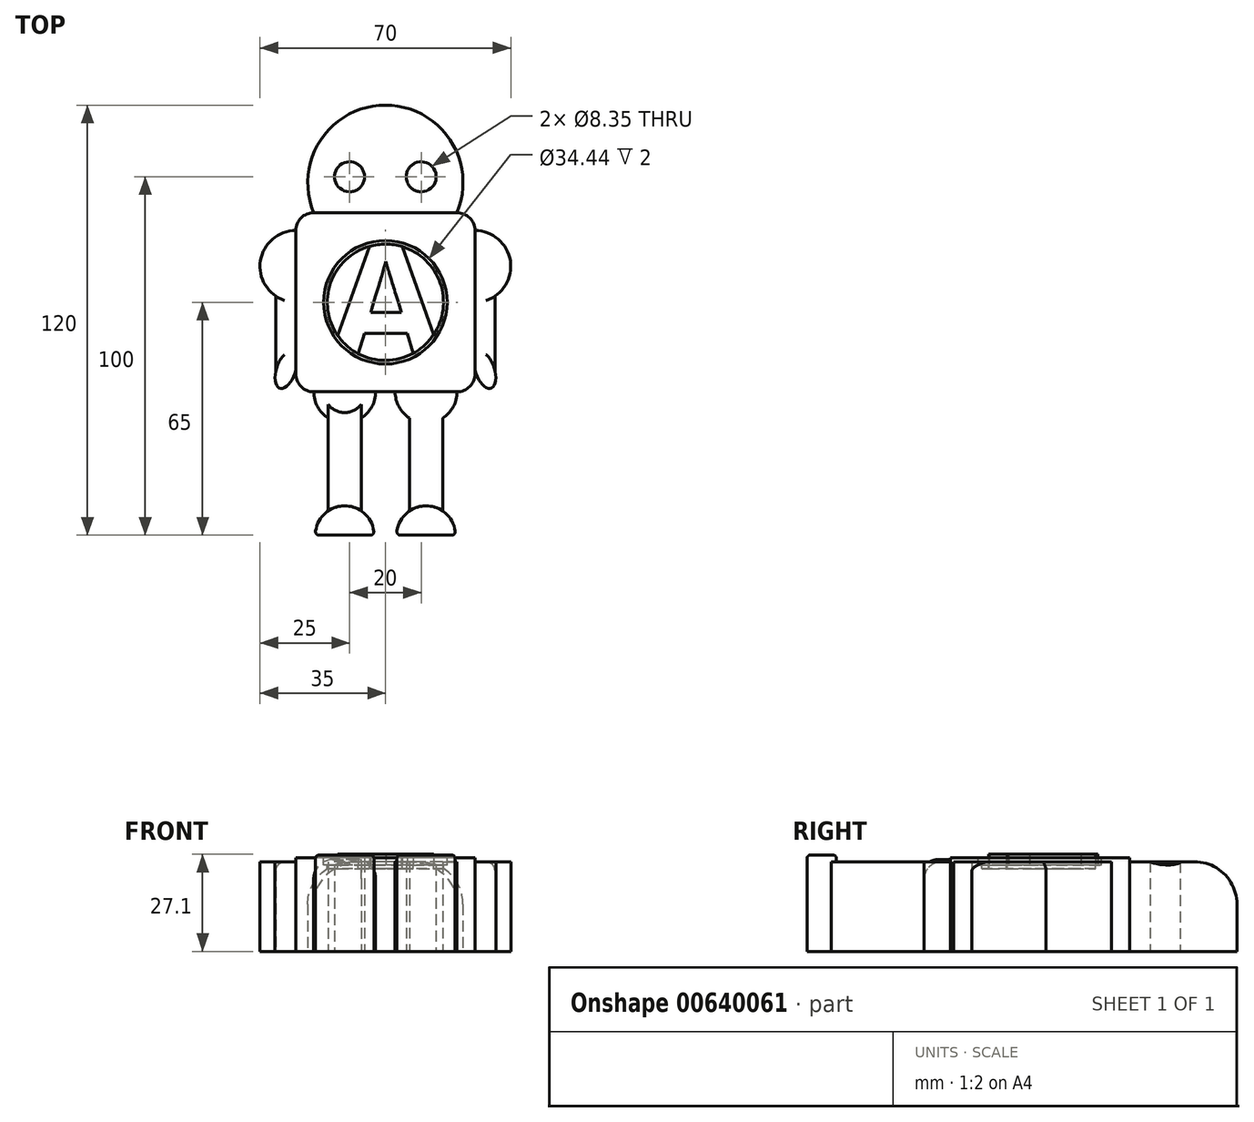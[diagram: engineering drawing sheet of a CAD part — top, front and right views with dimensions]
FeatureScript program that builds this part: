
annotation { "Feature Type Name" : "Feature", "Feature Type Description" : "" }
export const myFeature = defineFeature(function(context is Context, id is Id, definition is map)
    precondition{}
    {
        {
            var Q0;
            Q0=qCreatedBy(makeId("Top.planeOp"),FACE);
            var sketch = newSketch(context, id + "F0", { "sketchPlane" : qUnion([Q0])});
            skLineSegment(sketch, "E0.bottom", {"start": v(20, -25) * mm, "end": v(-20, -25) * mm});
            skLineSegment(sketch, "E0.top", {"start": v(20, 25) * mm, "end": v(-20, 25) * mm});
            skLineSegment(sketch, "E0.left", {"start": v(25, -20) * mm, "end": v(25, 20) * mm});
            skLineSegment(sketch, "E0.right", {"start": v(-25, -20) * mm, "end": v(-25, 20) * mm});
            skPoint(sketch, "E0.middle", {"position": v(0, 0) * mm});
            skPoint(sketch, "E1.visualSharp", {"position": v(-25, 25) * mm});
            skArc(sketch, "E1.filletArc", {"start": v(-20, 25) * mm, "mid": v(-23.54, 23.54) * mm, "end": v(-25, 20) * mm});
            skPoint(sketch, "E2.MirrorP", {"position": v(25, 25) * mm});
            skArc(sketch, "E3.MirrorCS", {"start": v(20, 25) * mm, "mid": v(23.54, 23.54) * mm, "end": v(25, 20) * mm});
            skArc(sketch, "E4.MirrorCS", {"start": v(20, -25) * mm, "mid": v(23.54, -23.54) * mm, "end": v(25, -20) * mm});
            skArc(sketch, "E5.MirrorCS", {"start": v(-20, -25) * mm, "mid": v(-23.54, -23.54) * mm, "end": v(-25, -20) * mm});
            skPoint(sketch, "E6.orphan", {"position": v(-25, -25) * mm});
            skPoint(sketch, "E7.orphan", {"position": v(25, -25) * mm});
            skArc(sketch, "E8", {"start": v(20, 25) * mm, "mid": v(0, 55) * mm, "end": v(-20, 25) * mm});
            skCircle(sketch, "E9", {"center": v(-10, 35) * mm, "radius": 4.18 * mm});
            skCircle(sketch, "E10.MirrorC", {"center": v(10, 35) * mm, "radius": 4.18 * mm});
            skArc(sketch, "E11", {"start": v(-25, 20) * mm, "mid": v(-34.57, 12.9) * mm, "end": v(-30.56, 1.69) * mm});
            skArc(sketch, "E12.MirrorCS", {"start": v(25, 20) * mm, "mid": v(34.57, 12.9) * mm, "end": v(30.56, 1.69) * mm});
            skLineSegment(sketch, "E13.left", {"start": v(-30.56, -18.96) * mm, "end": v(-30.56, 1.69) * mm});
            skPoint(sketch, "E13.middle", {"position": v(-25, -3.32) * mm});
            skLineSegment(sketch, "E14.MirrorCS", {"start": v(30.56, -18.96) * mm, "end": v(30.56, 1.69) * mm});
            skPoint(sketch, "E15.orphan", {"position": v(-30.56, 12.31) * mm});
            skPoint(sketch, "E16.orphan", {"position": v(-25, 0) * mm});
            skPoint(sketch, "E13.right.start.orphan", {"position": v(-19.44, -18.94) * mm});
            skPoint(sketch, "E13.top.end.orphan", {"position": v(-19.44, 12.33) * mm});
            skPoint(sketch, "E17.orphan", {"position": v(19.44, 12.33) * mm});
            skPoint(sketch, "E18.MirrorCS.start.orphan", {"position": v(30.56, 12.31) * mm});
            skPoint(sketch, "E19.orphan", {"position": v(25, 0) * mm});
            skPoint(sketch, "E20.MirrorCS.start.orphan", {"position": v(19.44, -18.94) * mm});
            skEllipticalArc(sketch, "E21", {});
            skEllipticalArc(sketch, "E22.MirrorC", {});
            skLineSegment(sketch, "E23.bottom", {"start": v(-6.75, -65) * mm, "end": v(-15.97, -65) * mm});
            skLineSegment(sketch, "E23.left", {"start": v(-6.75, -58.21) * mm, "end": v(-6.75, -32.3) * mm});
            skLineSegment(sketch, "E23.right", {"start": v(-15.97, -58.21) * mm, "end": v(-15.97, -32.3) * mm});
            skPoint(sketch, "E23.middle", {"position": v(-11.36, -43.9) * mm});
            skPoint(sketch, "E24.orphan", {"position": v(-2.71, -25) * mm});
            skPoint(sketch, "E25.MirrorCS.end.orphan", {"position": v(2.71, -25) * mm});
            skPoint(sketch, "E25.MirrorCS.start.orphan", {"position": v(20, -25) * mm});
            skArc(sketch, "E26", {"start": v(-20, -25) * mm, "mid": v(-11.36, -33.64) * mm, "end": v(-2.71, -25) * mm});
            skPoint(sketch, "E27.orphan", {"position": v(-15.97, -22.82) * mm});
            skPoint(sketch, "E28.trimOffspring.end.orphan", {"position": v(-6.75, -22.82) * mm});
            skArc(sketch, "E29.MirrorCS", {"start": v(20, -25) * mm, "mid": v(11.36, -33.64) * mm, "end": v(2.71, -25) * mm});
            skLineSegment(sketch, "E30.MirrorCS", {"start": v(6.75, -58.21) * mm, "end": v(6.75, -32.3) * mm});
            skLineSegment(sketch, "E31.MirrorCS", {"start": v(15.97, -58.21) * mm, "end": v(15.97, -32.3) * mm});
            skArc(sketch, "E32", {"start": v(-3.23, -63.86) * mm, "mid": v(-11.36, -56.8) * mm, "end": v(-19.48, -63.86) * mm});
            skLineSegment(sketch, "E33", {"start": v(-6.75, -65) * mm, "end": v(-4.22, -65) * mm});
            skLineSegment(sketch, "E34", {"start": v(-15.97, -65) * mm, "end": v(-18.5, -65) * mm});
            skArc(sketch, "E35.MirrorCS", {"start": v(3.23, -63.86) * mm, "mid": v(11.36, -56.8) * mm, "end": v(19.48, -63.86) * mm});
            skLineSegment(sketch, "E36.MirrorCS", {"start": v(6.75, -65) * mm, "end": v(4.22, -65) * mm});
            skLineSegment(sketch, "E37.MirrorCS", {"start": v(6.75, -65) * mm, "end": v(15.97, -65) * mm});
            skLineSegment(sketch, "E38.MirrorCS", {"start": v(15.97, -65) * mm, "end": v(18.5, -65) * mm});
            skPoint(sketch, "E39.orphan", {"position": v(6.75, -65) * mm});
            skPoint(sketch, "E40.orphan", {"position": v(15.97, -65) * mm});
            skPoint(sketch, "E41.visualSharp", {"position": v(-19.56, -65) * mm});
            skArc(sketch, "E41.filletArc", {"start": v(-19.48, -63.86) * mm, "mid": v(-19.25, -64.66) * mm, "end": v(-18.5, -65) * mm});
            skArc(sketch, "E42.MirrorCS", {"start": v(19.48, -63.86) * mm, "mid": v(19.25, -64.66) * mm, "end": v(18.5, -65) * mm});
            skPoint(sketch, "E43.orphan", {"position": v(19.56, -65) * mm});
            skPoint(sketch, "E44.visualSharp", {"position": v(-3.15, -65) * mm});
            skArc(sketch, "E44.filletArc", {"start": v(-4.22, -65) * mm, "mid": v(-3.47, -64.66) * mm, "end": v(-3.23, -63.86) * mm});
            skArc(sketch, "E45.MirrorCS", {"start": v(4.22, -65) * mm, "mid": v(3.47, -64.66) * mm, "end": v(3.23, -63.86) * mm});
            skPoint(sketch, "E46.orphan", {"position": v(3.15, -65) * mm});
            skLineSegment(sketch, "E47", {"start": v(27.78, -18.95) * mm, "end": v(29.49, -23.96) * mm, "construction": true});
            const initialGuessF0  = {"E21": [-0.02777802646160133, -0.01895405013479419, -0.3230569784827872, -0.9463795161844809, 0.005292489598687735, 0.0026651702230230663, 4.88466669376776, 1.7430740401779676], "E22.MirrorC": [0.02777802646160133, -0.01895405013479419, 0.32305697848278725, -0.946379516184481, 0.005292489598687735, 0.0026651702230230663, 4.5401112670016115, 1.3985186134118266]};
            skSetInitialGuess(sketch, initialGuessF0);
            skSolve(sketch);
        }
        {
            var Q0;
            Q0=makeQuery(id+"F0.imprint","IMPRINT",FACE,{"disambiguationData":[TD([[makeQuery(id+"F0.imprint","IMPRINT",EDGE,{"derivedFrom":sQuery(id+"F0.wireOp",EDGE,"E0.top")}),1.0]])]});
            extrude(context, id + "F1", {"entities" : qUnion([Q0]), "depth" : 26.1 * mm, "offsetDistance" : 25 * mm});
        }
        {
            var Q0;
            Q0 = qSketchRegion(id + "F0", true);
            extrude(context, id + "F2", {"entities" : qUnion([Q0]), "operationType" : NewBodyOperationType.ADD, "depth" : 25 * mm, "offsetDistance" : 25 * mm});
        }
        {
            var Q0;
            {var subQ0=sQuery(id+"F0.wireOp",EDGE,"E26");var subQ5=makeQuery(id+"F0.imprint","INTERSECT",VERTEX,{"derivedFrom":[sQuery(id+"F0.wireOp",EDGE,"E23.left"),subQ0]});Q0=makeQuery(id+"F0.imprint","IMPRINT",FACE,{"disambiguationData":[TD([[makeQuery(id+"F0.imprint","IMPRINT",EDGE,{"disambiguationData":[TD([[subQ5,1.0]])],"derivedFrom":subQ0}),1.0]])]});}
            var Q1;
            {var subQ0=sQuery(id+"F0.wireOp",EDGE,"E29.MirrorCS");var subQ5=makeQuery(id+"F0.imprint","INTERSECT",VERTEX,{"derivedFrom":[subQ0,sQuery(id+"F0.wireOp",EDGE,"E30.MirrorCS")]});Q1=makeQuery(id+"F0.imprint","IMPRINT",FACE,{"disambiguationData":[TD([[makeQuery(id+"F0.imprint","IMPRINT",EDGE,{"disambiguationData":[TD([[subQ5,1.0]])],"derivedFrom":subQ0}),-1.0]])]});}
            extrude(context, id + "F3", {"entities" : qUnion([Q0, Q1]), "operationType" : NewBodyOperationType.ADD, "depth" : 25.6 * mm, "offsetDistance" : 25 * mm});
        }
        {
            var Q0;
            Q0=makeQuery(id+"F0.imprint","IMPRINT",FACE,{"disambiguationData":[TD([[makeQuery(id+"F0.imprint","IMPRINT",EDGE,{"derivedFrom":sQuery(id+"F0.wireOp",EDGE,"E23.bottom")}),-1.0]])]});
            var Q1;
            Q1=makeQuery(id+"F0.imprint","IMPRINT",FACE,{"disambiguationData":[TD([[makeQuery(id+"F0.imprint","IMPRINT",EDGE,{"derivedFrom":sQuery(id+"F0.wireOp",EDGE,"E36.MirrorCS")}),-1.0]])]});
            extrude(context, id + "F4", {"entities" : qUnion([Q0, Q1]), "operationType" : NewBodyOperationType.ADD, "depth" : 26.9 * mm, "offsetDistance" : 25 * mm});
        }
        {
            var Q0;
            Q0=makeQuery(id+"F3.opExtrude","CAP_EDGE",EDGE,{"disambiguationData":[OSD([sQuery(id+"F0.wireOp",EDGE,"E29.MirrorCS")])],"isStart":false});
            var Q1;
            Q1=makeQuery(id+"F3.opExtrude","CAP_EDGE",EDGE,{"disambiguationData":[OSD([sQuery(id+"F0.wireOp",EDGE,"E26")])],"isStart":false});
            fillet(context, id + "F5", {"entities" : qUnion([Q0, Q1]), "radius" : 5.3 * mm, "tangentPropagation" : true, "allowEdgeOverflow" : false});
        }
        {
            var Q0;
            Q0=makeQuery(id+"F2.opExtrude","CAP_EDGE",EDGE,{"disambiguationData":[OSD([sQuery(id+"F0.wireOp",EDGE,"E8")])],"isStart":false});
            fillet(context, id + "F6", {"entities" : qUnion([Q0]), "radius" : 11.83 * mm, "allowEdgeOverflow" : false});
        }
        {
            var Q0;
            Q0=makeQuery(id+"F4.opExtrude","CAP_EDGE",EDGE,{"disambiguationData":[OSD([sQuery(id+"F0.wireOp",EDGE,"E32")])],"isStart":false});
            var Q1;
            Q1=makeQuery(id+"F4.opExtrude","CAP_EDGE",EDGE,{"disambiguationData":[OSD([sQuery(id+"F0.wireOp",EDGE,"E35.MirrorCS")])],"isStart":false});
            fillet(context, id + "F7", {"entities" : qUnion([Q0, Q1]), "radius" : 0.97 * mm, "tangentPropagation" : true, "allowEdgeOverflow" : false});
        }
        {
            var Q0;
            Q0=makeQuery(id+"F2.opExtrude","CAP_EDGE",EDGE,{"disambiguationData":[OSD([sQuery(id+"F0.wireOp",EDGE,"E13.left")])],"isStart":false});
            var Q1;
            Q1=makeQuery(id+"F2.opExtrude","CAP_EDGE",EDGE,{"disambiguationData":[OSD([sQuery(id+"F0.wireOp",EDGE,"E14.MirrorCS")])],"isStart":false});
            fillet(context, id + "F8", {"entities" : qUnion([Q0, Q1]), "radius" : 2.41 * mm, "tangentPropagation" : true, "allowEdgeOverflow" : false});
        }
        {
            var Q0;
            Q0=makeQuery(id+"F1.opExtrude","CAP_FACE",FACE,{"disambiguationData":[OSD([sQuery(id+"F0.wireOp",EDGE,"E0.bottom"),sQuery(id+"F0.wireOp",EDGE,"E0.top"),sQuery(id+"F0.wireOp",EDGE,"E0.left"),sQuery(id+"F0.wireOp",EDGE,"E0.right"),sQuery(id+"F0.wireOp",EDGE,"E1.filletArc"),sQuery(id+"F0.wireOp",EDGE,"E3.MirrorCS"),sQuery(id+"F0.wireOp",EDGE,"E4.MirrorCS"),sQuery(id+"F0.wireOp",EDGE,"E5.MirrorCS")])],"isStart":false});
            var sketch = newSketch(context, id + "F9", { "sketchPlane" : qUnion([Q0])});
            skCircle(sketch, "E48", {"center": v(0, 0) * mm, "radius": 17.22 * mm});
            skCircle(sketch, "E49.0", {"center": v(0, 0) * mm, "radius": 16.22 * mm});
            skText(sketch, "E50", { "text": "A\n", "fontName": "OpenSans-Bold.ttf"});
            const initialGuessF9  = {"E50": [-0.01578, -0.01652, 1, 0, 0.0332]};
            skSetInitialGuess(sketch, initialGuessF9);
            skSolve(sketch);
        }
        {
            var Q0;
            {var subQ6=sQuery(id+"F9.wireOp",EDGE,"E50.sketch_text.stroke-1");Q0=makeQuery(id+"F9.imprint","IMPRINT",FACE,{"disambiguationData":[TD([[makeQuery(id+"F9.imprint","IMPRINT",EDGE,{"derivedFrom":subQ6}),-1.0]])]});}
            extrude(context, id + "F10", {"entities" : qUnion([Q0]), "operationType" : NewBodyOperationType.ADD, "depth" : 1 * mm, "offsetDistance" : 25 * mm});
        }
        {
            var Q0;
            {var subQ10=sQuery(id+"F9.wireOp",EDGE,"E50.sketch_text.stroke-5");Q0=makeQuery(id+"F9.imprint","IMPRINT",FACE,{"disambiguationData":[TD([[makeQuery(id+"F9.imprint","IMPRINT",EDGE,{"derivedFrom":subQ10}),1.0]])]});}
            var Q1;
            {var subQ5=sQuery(id+"F9.wireOp",EDGE,"E50.sketch_text.stroke-5");Q1=makeQuery(id+"F9.imprint","IMPRINT",FACE,{"disambiguationData":[TD([[makeQuery(id+"F9.imprint","IMPRINT",EDGE,{"derivedFrom":subQ5}),-1.0]])]});}
            var Q2;
            {var subQ0=sQuery(id+"F9.wireOp",EDGE,"E50.sketch_text.stroke-2");var subQ1=sQuery(id+"F9.wireOp",EDGE,"E48");var subQ2=makeQuery(id+"F9.imprint","INTERSECT",VERTEX,{"derivedFrom":[subQ1,subQ0]});Q2=makeQuery(id+"F9.imprint","IMPRINT",FACE,{"disambiguationData":[TD([[makeQuery(id+"F9.imprint","IMPRINT",EDGE,{"disambiguationData":[TD([[subQ2,1.0]])],"derivedFrom":subQ1}),1.0]])]});}
            var Q3;
            {var subQ0=sQuery(id+"F9.wireOp",EDGE,"E50.sketch_text.stroke-2");var subQ1=sQuery(id+"F9.wireOp",EDGE,"E48");var subQ2=makeQuery(id+"F9.imprint","INTERSECT",VERTEX,{"derivedFrom":[subQ1,subQ0]});Q3=makeQuery(id+"F9.imprint","IMPRINT",FACE,{"disambiguationData":[TD([[makeQuery(id+"F9.imprint","IMPRINT",EDGE,{"disambiguationData":[TD([[subQ2,-1.0]])],"derivedFrom":subQ1}),1.0]])]});}
            var Q4;
            {var subQ0=sQuery(id+"F9.wireOp",EDGE,"E50.sketch_text.stroke-0");var subQ1=sQuery(id+"F9.wireOp",EDGE,"E48");var subQ2=makeQuery(id+"F9.imprint","INTERSECT",VERTEX,{"derivedFrom":[subQ1,subQ0]});Q4=makeQuery(id+"F9.imprint","IMPRINT",FACE,{"disambiguationData":[TD([[makeQuery(id+"F9.imprint","IMPRINT",EDGE,{"disambiguationData":[TD([[subQ2,-1.0]])],"derivedFrom":subQ1}),1.0]])]});}
            extrude(context, id + "F11", {"entities" : qUnion([Q0, Q1, Q2, Q3, Q4]), "operationType" : NewBodyOperationType.REMOVE, "oppositeDirection" : true, "depth" : 2 * mm, "offsetDistance" : 25 * mm});
        }
        {
            var Q0;
            {var subQ4=sQuery(id+"F9.wireOp",EDGE,"E50.sketch_text.stroke-4");var subQ5=makeQuery(id+"F10.opExtrude","SWEPT_FACE",FACE,{"disambiguationData":[OSD([subQ4])]});var subQ9=sQuery(id+"F0.wireOp",EDGE,"E5.MirrorCS");var subQ10=sQuery(id+"F0.wireOp",EDGE,"E4.MirrorCS");var subQ11=sQuery(id+"F0.wireOp",EDGE,"E3.MirrorCS");var subQ12=sQuery(id+"F0.wireOp",EDGE,"E1.filletArc");var subQ13=sQuery(id+"F0.wireOp",EDGE,"E0.right");var subQ14=sQuery(id+"F0.wireOp",EDGE,"E0.bottom");var subQ15=sQuery(id+"F0.wireOp",EDGE,"E0.top");var subQ16=sQuery(id+"F0.wireOp",EDGE,"E0.left");Q0=makeQuery(id+"F11.boolean.opBoolean","SPLIT",FACE,{"disambiguationData":[TD([subQ5])],"derivedFrom":makeQuery(id+"F10.boolean.opBoolean","SPLIT",FACE,{"disambiguationData":[TD([makeQuery(id+"F1.opExtrude","SWEPT_FACE",FACE,{"disambiguationData":[OSD([subQ14])]})])],"derivedFrom":makeQuery(id+"F1.opExtrude","CAP_FACE",FACE,{"disambiguationData":[OSD([subQ14,subQ15,subQ16,subQ13,subQ12,subQ11,subQ10,subQ9])],"isStart":false})})});}
            var Q1;
            {var subQ0=sQuery(id+"F9.wireOp",EDGE,"E50.sketch_text.stroke-6");var subQ1=makeQuery(id+"F10.opExtrude","SWEPT_FACE",FACE,{"disambiguationData":[OSD([subQ0])]});var subQ9=sQuery(id+"F0.wireOp",EDGE,"E5.MirrorCS");var subQ10=sQuery(id+"F0.wireOp",EDGE,"E4.MirrorCS");var subQ11=sQuery(id+"F0.wireOp",EDGE,"E3.MirrorCS");var subQ12=sQuery(id+"F0.wireOp",EDGE,"E1.filletArc");var subQ13=sQuery(id+"F0.wireOp",EDGE,"E0.right");var subQ14=sQuery(id+"F0.wireOp",EDGE,"E0.bottom");var subQ15=sQuery(id+"F0.wireOp",EDGE,"E0.top");var subQ16=sQuery(id+"F0.wireOp",EDGE,"E0.left");Q1=makeQuery(id+"F11.boolean.opBoolean","SPLIT",FACE,{"disambiguationData":[TD([subQ1])],"derivedFrom":makeQuery(id+"F10.boolean.opBoolean","SPLIT",FACE,{"disambiguationData":[TD([makeQuery(id+"F1.opExtrude","SWEPT_FACE",FACE,{"disambiguationData":[OSD([subQ14])]})])],"derivedFrom":makeQuery(id+"F1.opExtrude","CAP_FACE",FACE,{"disambiguationData":[OSD([subQ14,subQ15,subQ16,subQ13,subQ12,subQ11,subQ10,subQ9])],"isStart":false})})});}
            var Q2;
            Q2=makeQuery(id+"F10.boolean.opBoolean","SPLIT",FACE,{"disambiguationData":[TD([makeQuery(id+"F10.opExtrude","SWEPT_FACE",FACE,{"disambiguationData":[OSD([sQuery(id+"F9.wireOp",EDGE,"E50.sketch_text.stroke-8")])]})])],"derivedFrom":makeQuery(id+"F1.opExtrude","CAP_FACE",FACE,{"disambiguationData":[OSD([sQuery(id+"F0.wireOp",EDGE,"E0.bottom"),sQuery(id+"F0.wireOp",EDGE,"E0.top"),sQuery(id+"F0.wireOp",EDGE,"E0.left"),sQuery(id+"F0.wireOp",EDGE,"E0.right"),sQuery(id+"F0.wireOp",EDGE,"E1.filletArc"),sQuery(id+"F0.wireOp",EDGE,"E3.MirrorCS"),sQuery(id+"F0.wireOp",EDGE,"E4.MirrorCS"),sQuery(id+"F0.wireOp",EDGE,"E5.MirrorCS")])],"isStart":false})});
            var Q3;
            {var subQ0=sQuery(id+"F9.wireOp",EDGE,"E50.sketch_text.stroke-0");var subQ7=makeQuery(id+"F10.opExtrude","SWEPT_FACE",FACE,{"disambiguationData":[OSD([subQ0])]});var subQ11=sQuery(id+"F0.wireOp",EDGE,"E5.MirrorCS");var subQ12=sQuery(id+"F0.wireOp",EDGE,"E4.MirrorCS");var subQ13=sQuery(id+"F0.wireOp",EDGE,"E3.MirrorCS");var subQ14=sQuery(id+"F0.wireOp",EDGE,"E1.filletArc");var subQ15=sQuery(id+"F0.wireOp",EDGE,"E0.right");var subQ16=sQuery(id+"F0.wireOp",EDGE,"E0.bottom");var subQ17=sQuery(id+"F0.wireOp",EDGE,"E0.top");var subQ18=sQuery(id+"F0.wireOp",EDGE,"E0.left");Q3=makeQuery(id+"F11.boolean.opBoolean","SPLIT",FACE,{"disambiguationData":[TD([subQ7])],"derivedFrom":makeQuery(id+"F10.boolean.opBoolean","SPLIT",FACE,{"disambiguationData":[TD([makeQuery(id+"F1.opExtrude","SWEPT_FACE",FACE,{"disambiguationData":[OSD([subQ16])]})])],"derivedFrom":makeQuery(id+"F1.opExtrude","CAP_FACE",FACE,{"disambiguationData":[OSD([subQ16,subQ17,subQ18,subQ15,subQ14,subQ13,subQ12,subQ11])],"isStart":false})})});}
            extrude(context, id + "F12", {"entities" : qUnion([Q0, Q1, Q2, Q3]), "operationType" : NewBodyOperationType.REMOVE, "oppositeDirection" : true, "depth" : 3 * mm, "offsetDistance" : 25 * mm});
        }
    });
